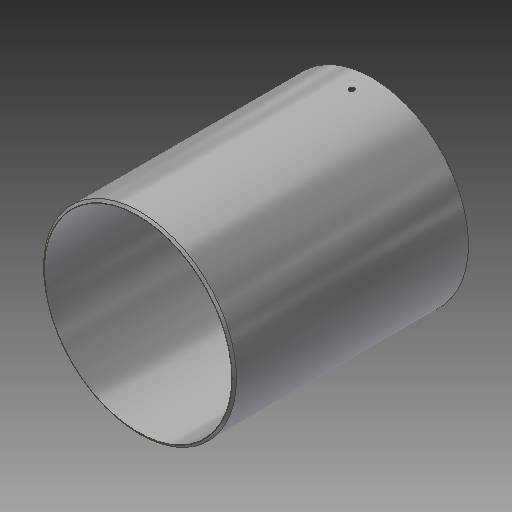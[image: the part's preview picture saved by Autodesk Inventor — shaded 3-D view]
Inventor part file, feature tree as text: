
AUTODESK INVENTOR PART (.ipt)
format: ipt  version: 2017.3 (Build 213257000, 257)  size: 215,040 bytes
history: native  units: in
note: dims shown in document units (in); Inventor stores cm internally (conversion verified against a paired STEP export)
features: chamfer x2, sketch x2, extrude x1, plane x1, hole x1, pattern_circular x1
ambient origin geometry x8: Origin, YZ Plane, XZ Plane, XY Plane, X Axis, Y Axis, Z Axis, Center Point
bodies: Solid1 (feature_tree)
feature tree (8):
  extrude  "Extrusion1"  Depth=33.0in
  chamfer  "Chamfer1"  Distance=41.5536in
  chamfer  "Chamfer2"  Distance=0.125in
  plane  "Work Plane1"
  hole  "Hole1"  [1 undecoded]
  pattern_circular  "Circular Pattern1"  [2 undecoded]
  sketch  "Sketch1"  dims[d0=34.0in d1=33.0in d2=41.5536in d3=0.0in]
  sketch  "Sketch2"  dims[d4=0.4375in d5=0.125in d6=0.2577in d7=0.4375in d8=0.125in d9=0.2577in d10=3.9062in d11=0.891in d12=0.553in d13=0.0246in d14=0.897in d15=0.375in d16=0.25in d17=0.5635in d18=0.91in d19=0.8108in d20=0.7874in d21=360.0deg]
note: 3 required parameter values undecoded (feature->parameter linkage not recoverable at this tier; creation-order binding heuristic only, values carry confidence <= 0.55)
